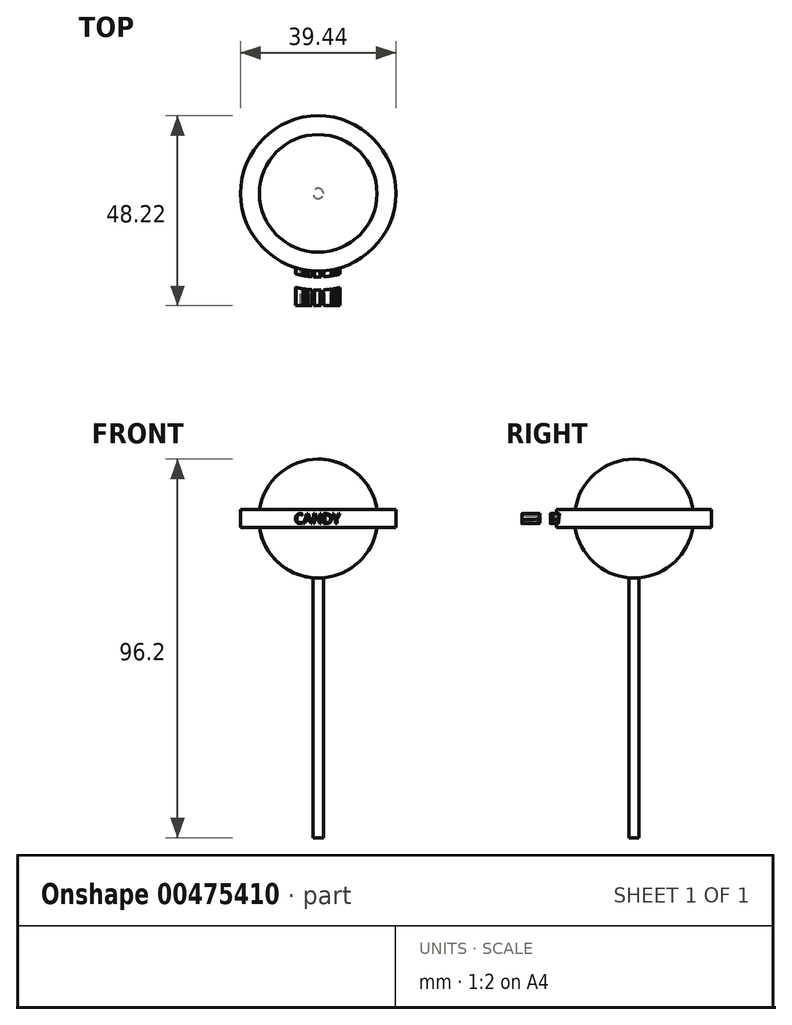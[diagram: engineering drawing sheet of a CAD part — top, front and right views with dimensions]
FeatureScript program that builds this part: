
annotation { "Feature Type Name" : "Feature", "Feature Type Description" : "" }
export const myFeature = defineFeature(function(context is Context, id is Id, definition is map)
    precondition{}
    {
        {
            var Q0;
            Q0=qCreatedBy(makeId("Front.planeOp"),FACE);
            var sketch = newSketch(context, id + "F0", { "sketchPlane" : qUnion([Q0])});
            skArc(sketch, "E0", {"start": v(0, -15.1) * mm, "mid": v(15.1, 0) * mm, "end": v(0, 15.1) * mm});
            skLineSegment(sketch, "E1", {"start": v(0, 15.1) * mm, "end": v(0, -15.1) * mm});
            skLineSegment(sketch, "E2", {"start": v(0, 0) * mm, "end": v(0, 35.8) * mm, "construction": true});
            skLineSegment(sketch, "E3.bottom", {"start": v(19.72, 2.25) * mm, "end": v(5.79, 2.25) * mm});
            skLineSegment(sketch, "E3.top", {"start": v(19.72, -2.25) * mm, "end": v(5.79, -2.25) * mm});
            skLineSegment(sketch, "E3.left", {"start": v(19.72, 2.25) * mm, "end": v(19.72, -2.25) * mm});
            skLineSegment(sketch, "E3.right", {"start": v(5.79, 2.25) * mm, "end": v(5.79, -2.25) * mm});
            skPoint(sketch, "E3.middle", {"position": v(12.76, 0) * mm});
            skLineSegment(sketch, "E4.bottom", {"start": v(0, -12.36) * mm, "end": v(1.31, -12.36) * mm});
            skLineSegment(sketch, "E4.top", {"start": v(0, -81.09) * mm, "end": v(1.31, -81.09) * mm});
            skLineSegment(sketch, "E4.left", {"start": v(0, -12.36) * mm, "end": v(0, -81.09) * mm});
            skLineSegment(sketch, "E4.right", {"start": v(1.31, -12.36) * mm, "end": v(1.31, -81.09) * mm});
            skSolve(sketch);
        }
        {
            var Q0;
            Q0 = qSketchRegion(id + "F0", true);
            var Q1;
            Q1=sQuery(id+"F0.wireOp",EDGE,"E2");
            revolve(context, id + "F1", {"entities" : qUnion([Q0]), "axis" : qUnion([Q1]), "revolveType" : RevolveType.FULL});
        }
        {
            var Q0;
            Q0=qCreatedBy(makeId("Front.planeOp"),FACE);
            var sketch = newSketch(context, id + "F2", { "sketchPlane" : qUnion([Q0])});
            skText(sketch, "E5", { "text": "CANDY", "fontName": "OpenSans-Regular.ttf"});
            const initialGuessF2  = {"E5": [-0.00597, -0.00126, 1, 0, 0.00251]};
            skSetInitialGuess(sketch, initialGuessF2);
            skSolve(sketch);
        }
        {
            var Q0;
            Q0 = qSketchRegion(id + "F2", true);
            extrude(context, id + "F3", {"entities" : qUnion([Q0]), "operationType" : NewBodyOperationType.ADD, "depth" : 28.5 * mm});
        }
        {
            var Q0;
            Q0=qCreatedBy(makeId("Front.planeOp"),FACE);
            var sketch = newSketch(context, id + "F4", { "sketchPlane" : qUnion([Q0])});
            skLineSegment(sketch, "E6", {"start": v(19.72, 2.25) * mm, "end": v(19.72, -2.25) * mm});
            skLineSegment(sketch, "E7.0", {"start": v(21.22, -3.75) * mm, "end": v(14.87, -3.75) * mm});
            skLineSegment(sketch, "E7.1", {"start": v(21.22, 3.75) * mm, "end": v(21.22, -3.75) * mm});
            skLineSegment(sketch, "E7.2", {"start": v(21.22, 3.75) * mm, "end": v(15.58, 3.75) * mm});
            skLineSegment(sketch, "E8", {"start": v(15.58, 3.75) * mm, "end": v(13.79, 9.54) * mm});
            skLineSegment(sketch, "E9", {"start": v(13.79, 9.54) * mm, "end": v(24.55, 9.54) * mm});
            skLineSegment(sketch, "E10", {"start": v(24.55, 9.54) * mm, "end": v(24.55, -7.67) * mm});
            skLineSegment(sketch, "E11", {"start": v(24.55, -7.67) * mm, "end": v(14.87, -3.75) * mm});
            skSolve(sketch);
        }
        {
            var Q0;
            Q0=qCreatedBy(makeId("Front.planeOp"),FACE);
            var sketch = newSketch(context, id + "F5", { "sketchPlane" : qUnion([Q0])});
            skLineSegment(sketch, "E12", {"start": v(0, 0) * mm, "end": v(0, 44.95) * mm, "construction": true});
            skSolve(sketch);
        }
        {
            var Q0;
            Q0 = qSketchRegion(id + "F4", true);
            var Q1;
            Q1=sQuery(id+"F5.wireOp",EDGE,"E12");
            revolve(context, id + "F6", {"operationType" : NewBodyOperationType.REMOVE, "entities" : qUnion([Q0]), "axis" : qUnion([Q1]), "revolveType" : RevolveType.FULL, "oppositeDirection" : true});
        }
    });
